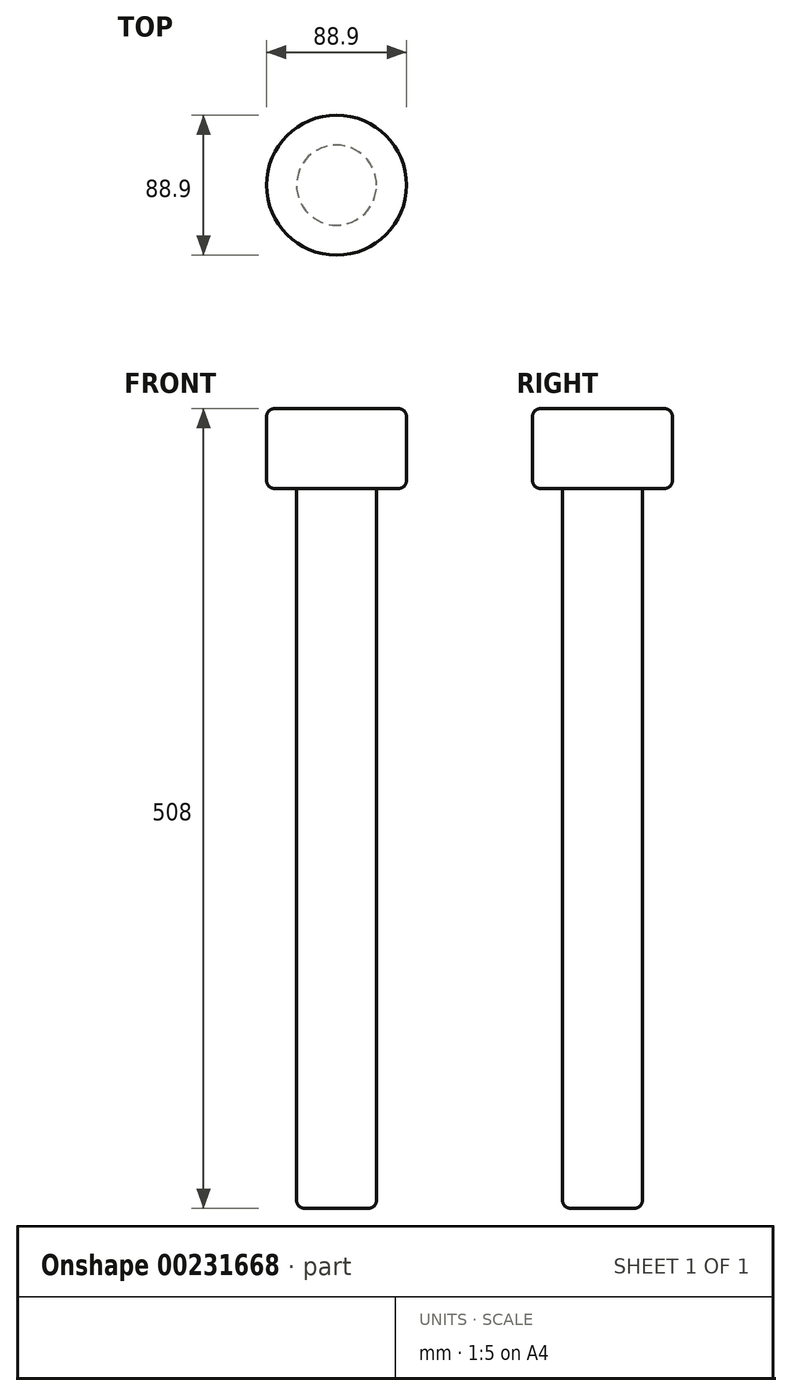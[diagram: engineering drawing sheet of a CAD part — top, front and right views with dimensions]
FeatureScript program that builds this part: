
annotation { "Feature Type Name" : "Feature", "Feature Type Description" : "" }
export const myFeature = defineFeature(function(context is Context, id is Id, definition is map)
    precondition{}
    {
        {
            var Q0;
            Q0=qCreatedBy(makeId("Top.planeOp"),FACE);
            var sketch = newSketch(context, id + "F0", { "sketchPlane" : qUnion([Q0])});
            skCircle(sketch, "E0", {"center": v(0, 0) * mm, "radius": 25.4 * mm});
            skCircle(sketch, "E1", {"center": v(0, 0) * mm, "radius": 44.45 * mm});
            skSolve(sketch);
        }
        {
            var Q0;
            Q0=makeQuery(id+"F0.imprint","IMPRINT",FACE,{"disambiguationData":[TD([[makeQuery(id+"F0.imprint","IMPRINT",EDGE,{"derivedFrom":sQuery(id+"F0.wireOp",EDGE,"E0")}),1.0]])]});
            extrude(context, id + "F1", {"entities" : qUnion([Q0]), "oppositeDirection" : true, "depth" : 508 * mm});
        }
        {
            var Q0;
            Q0=makeQuery(id+"F0.imprint","IMPRINT",FACE,{"disambiguationData":[TD([[makeQuery(id+"F0.imprint","IMPRINT",EDGE,{"derivedFrom":sQuery(id+"F0.wireOp",EDGE,"E0")}),-1.0]])]});
            extrude(context, id + "F2", {"entities" : qUnion([Q0]), "operationType" : NewBodyOperationType.ADD, "oppositeDirection" : true, "depth" : 50.8 * mm});
        }
        {
            var Q0;
            Q0=makeQuery(id+"F2.opExtrude","CAP_EDGE",EDGE,{"disambiguationData":[OSD([sQuery(id+"F0.wireOp",EDGE,"E1")])],"isStart":false});
            var Q1;
            Q1=makeQuery(id+"F2.opExtrude","CAP_EDGE",EDGE,{"disambiguationData":[OSD([sQuery(id+"F0.wireOp",EDGE,"E1")])],"isStart":true});
            var Q2;
            Q2=makeQuery(id+"F1.opExtrude","CAP_EDGE",EDGE,{"disambiguationData":[OSD([sQuery(id+"F0.wireOp",EDGE,"E0")])],"isStart":false});
            fillet(context, id + "F3", {"entities" : qUnion([Q0, Q1, Q2]), "radius" : 5.08 * mm, "tangentPropagation" : true, "allowEdgeOverflow" : false});
        }
    });
